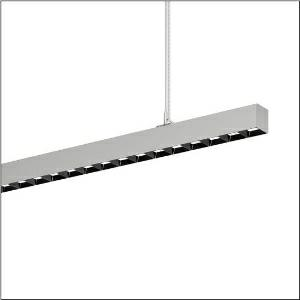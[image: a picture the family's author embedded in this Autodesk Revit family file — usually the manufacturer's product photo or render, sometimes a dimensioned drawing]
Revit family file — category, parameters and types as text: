
# Revit family: silica_r__21_51mx34dc3dsb_1a3f
name_source: partatom
category: Lighting Fixtures
units: mm (PartAtom-declared; Revit-internal decimal feet)

## family parameters
Cut with Voids When Loaded = No
Host = Face
Light Source = No
Part Type = Normal
Room Calculation Point = No
Round Connector Dimension = Use Diameter
Shared = No

## types (1)
- --- (1 x LED, 19200 lm, 129.1 W, 3000K)
    Apparent Load = 129 VA
    CIE Flux Codes = 74 94 99 56 100
    Color Rendering = 80
    Color Temperature = 3000K
    Default Elevation = 1800 mm
    Description = Silica® 21, office luminaire, primary light control with darklight reflector, of PMMA, black, light emission: direct/indirect distribution, primary light characteristic: asymmetric, installation type: suspended mounting, LED, rated luminous flux: 19.200lm, luminous efficacy: 149lm/W, light colour: 830, colour temperature: 3000K, control gear: DALI 2, with terminal, 3+2-pole, max. 2.5mm², mains connection: 220..240V, AC, 50/60Hz, rated input power: 129.1W, luminaire housing, of aluminium, metallic grey (RAL 9006), length: 3.004mm, width: 53mm, height: 53mm, protection rating (complete): IP20, insulation class (complete): insulation class I (protective earthing), certification: CE, permissible operating ambient temperature: 0..+35°C, standard: EN 50419, packaging unit: 1 piece
    Height = 53 mm
    Lamp = 1 x LED
    Lamp Light Flux = 19200 lm
    Lamp Power = 129.1 W
    Lamp count = 1
    Length = 3004 mm
    Luminous efficacy = 149 lm/W
    Manufacturer = Siteco
    ModVariant = No
    Model = 51MX34DC3DSB
    Mounting Place = Ceiling
    Mounting Type = Pendant
    Number of Poles = 1
    OnlyDefault = Yes
    Power Factor = 1
    Product Name = Silica® 21
    Product group = office luminaire | ceiling pendant
    ProductGroupID = 904
    Protection Class = Protection class I
    Protection Degree = IP 20
    RLX_Detail_Level = 1
    RLX_Emergency_Light_Flux = 0 lm
    RLX_Emergency_Type = 0
    RLX_Emergency_Type_DB = No
    RlxData = <blob elided: 67509 chars, md5=77a99e62>
    Socket = socket
    Standby Power = 0 W
    System Light Flux = 19200 lm
    System Power = 129 W
    Type Comments = factory setting: luminous flux: 100 % | dim-lin: 254 | 448 mA
    Type Image = l_1335859.jpg
    URL = http://relux.com
    VarID = @adj_119842
    Voltage = 0 V
    Weight = 0.00 kg
    Width = 53 mm

## geometry (parser evidence)
native form markers: Blend x4, Sweep x12
no freeform markers — native parametric forms only
